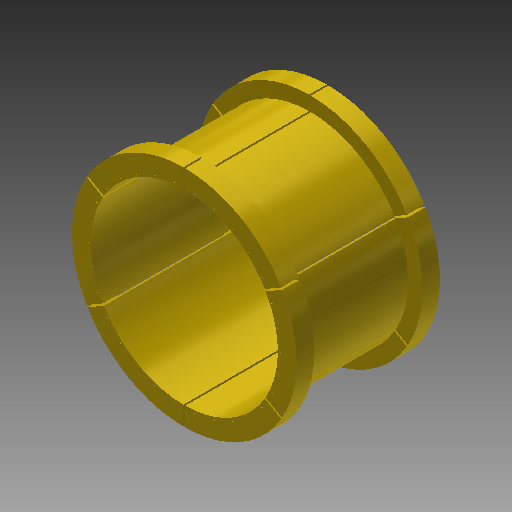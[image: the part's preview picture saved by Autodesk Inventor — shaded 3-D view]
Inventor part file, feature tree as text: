
AUTODESK INVENTOR PART (.ipt)
format: ipt  version: 2017 (Build 210142000, 142)  size: 457,728 bytes
history: native  units: mm (DEFAULTED — no unit token found)
features: sketch x13, extrude x10, pattern_circular x3, revolve x2, projected_geometry x1
ambient origin geometry x8: Origin, YZ Plane, XZ Plane, XY Plane, X Axis, Y Axis, Z Axis, Center Point
bodies: Solid1 (feature_tree)
feature tree (29):
  extrude  "Extrusion1"  Depth=210.7mm
  sketch  "Sketch2"  dims[d2=154.0mm d3=0.0mm d5=1.0mm d6=60.0mm d8=360.0deg]
  extrude  "Extrusion2"  Depth=1.0mm
  pattern_circular  "Circular Pattern1"  Count=6 Angle=360.0deg
  extrude  "Extrusion4"  Depth=155.0mm TaperAngle=0.0deg
  extrude  "Extrusion3"  Depth=0.5mm
  revolve  "Revolution1"  Angle=90.0deg
  pattern_circular  "Circular Pattern2"  Count=30 Angle=360.0deg
  revolve  "Revolution2"  [1 undecoded]
  pattern_circular  "Circular Pattern3"  Count=30 Angle=360.0deg
  extrude  "Extrusion5"  Depth=206.7mm
  extrude  "Extrusion6"  Depth=18.9992mm
  extrude  "Extrusion7"  Depth=18.9992mm TaperAngle=0.0deg
  extrude  "Extrusion8"  Depth=155.0mm TaperAngle=0.0deg
  extrude  "Extrusion9"  Depth=155.0mm TaperAngle=0.0deg
  extrude  "Extrusion10"  Depth=102.85mm TaperAngle=0.0deg
  sketch  "Sketch1"  dims[d0=200.7mm d1=210.7mm]
  sketch  "Sketch3"  dims[d10=60.0mm d12=360.0deg d14=155.0mm d15=0.0mm]
  sketch  "Sketch4"  dims[d16=60.0mm d17=360.0deg d20=0.5mm]
  sketch  "Sketch5"  dims[d21=2.0mm d22=90.0deg d23=300.0mm d24=360.0deg]
  sketch  "Sketch6"  dims[d27=0.5mm d28=2.0mm]
  sketch  "Sketch7"  dims[d29=90.0deg d30=300.0mm d31=360.0deg]
  sketch  "Sketch8"  dims[d33=241.3mm d34=206.7mm]
  sketch  "Sketch9"  dims[d35=18.9992mm d36=0.0mm d37=206.7mm]
  sketch  "Sketch10"  dims[d38=241.3mm d39=18.9992mm d40=0.0mm]
  sketch  "Sketch11"  dims[d41=155.0mm d42=0.0mm d43=155.0mm d44=0.0mm]
  sketch  "Sketch12"  dims[d45=155.0mm d46=0.0mm d47=155.0mm d48=0.0mm]
  sketch  "Sketch13"  dims[d49=155.0mm d50=0.0mm d51=155.0mm d52=0.0mm d53=102.85mm d54=102.85mm]
  projected_geometry  "Projected Loop1"
note: 1 required parameter value undecoded (feature->parameter linkage not recoverable at this tier; creation-order binding heuristic only, values carry confidence <= 0.55)
